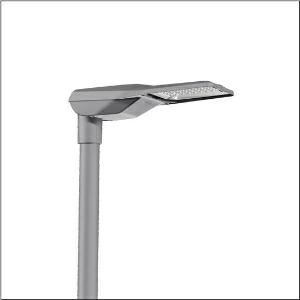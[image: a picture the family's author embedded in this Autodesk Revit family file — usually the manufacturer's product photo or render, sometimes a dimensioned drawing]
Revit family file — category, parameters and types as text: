
# Revit family: streetlight_sl_21_iq_mini___stw1_0a_5xe2e41g08hb_6f26
name_source: partatom
category: Lighting Fixtures
units: mm (PartAtom-declared; Revit-internal decimal feet)

## family parameters
Cut with Voids When Loaded = No
Host = Face
Light Source = No
Part Type = Normal
Room Calculation Point = No
Round Connector Dimension = Use Diameter
Shared = No

## types (1)
- --- (1 x LED, 9860 lm, 70.9 W, 4000K)
    Apparent Load = 71 VA
    CIE Flux Codes = 38 75 98 100 100
    Color Rendering = 70
    Color Temperature = 4000K
    Default Elevation = 1800 mm
    Description = Streetlight SL 21 iQ mini, mast luminaire, primary light control with lens, of PMMA, primary optical cover: cover, of toughened safety glass, transparent, light distribution: STW1.0a, light emission: direct distribution, primary light characteristic: asymmetric, installation type: post-top, side-entry, LED, High Power LED, rated luminous flux: 9.860lm, luminous efficacy: 139lm/W, light colour: 740, colour temperature: 4000K, control: Street-Remote, Auto-Match, Temp-Guard, Lumen-Switch, Night-Set, Smart-Wire, Light-Fading, Desk-Remote (wireless, voltage-free reading and setting of iQ features in the workshop via application-optimized NFC function/RFID function), optimised constant luminous flux control (CLO 2.0), presetting dimming linear, mains connection: 220..240V, AC, 50/60Hz, start of lifetime: 71W, end of service life: 75W, reduction: 31W, luminaire housing, of diecast aluminium, powder-coated, Siteco® metallic grey (DB 702S), corrosivity category C5 mid according to DIN EN ISO 12944, please order mast flange separately, inclination adjustable: 0°, 5°, 10°, 15°, sealing non-destructively replaceable, multi-level sealing system, length: 628mm, width: 235mm, height: 110mm, mast flange for spigot size: 42mm (side-entry): 5XC10008XM4, 60/48mm (side-entry/post-top): 5XC10108XM2, 76/60mm (side-entry/post-top): 5XC10108XM1, protection rating (complete): IP66, insulation class (complete): insulation class II (safety insulation), certification: CE, ENEC, ENEC+, VDE, impact resistance: IK09, permissible operating ambient temperature for outdoor applications: -40..+50°C, standard-compliant lighting for roads and squares, packaging unit: 1 piece

Light Distribution: STW1.0a
    Height = 110 mm
    Lamp = 1 x LED
    Lamp Light Flux = 9860 lm
    Lamp Power = 70.9 W
    Lamp count = 1
    Length = 625 mm
    Luminous efficacy = 139 lm/W
    Manufacturer = Siteco
    ModVariant = No
    Model = 5XE2E41G08HB
    Number of Poles = 1
    OnlyDefault = Yes
    Power Factor = 1
    Product Name = Streetlight SL 21 iQ mini | STW1.0a
    Product group = mast luminaire | pylon top
    ProductGroupID = 6100
    Protection Class = Protection class II
    Protection Degree = IP 66
    RLX_Detail_Level = 1
    RLX_Emergency_Light_Flux = 0 lm
    RLX_Emergency_Type = 0
    RLX_Emergency_Type_DB = No
    RlxData = <blob elided: 92297 chars, md5=34aeb5c1>
    Socket = socket
    Standby Power = 0 W
    System Light Flux = 9860 lm
    System Power = 71 W
    Type Comments = factory setting: luminous flux: 100 % | dim-lin: 254 | 711 mA
    Type Image = l_1003519.jpg
    URL = http://relux.com
    VarID = @adj_107929
    Voltage = 0 V
    Weight = 0.00 kg
    Width = 234 mm

## geometry (parser evidence)
native form markers: Blend x4, Sweep x13
no freeform markers — native parametric forms only
